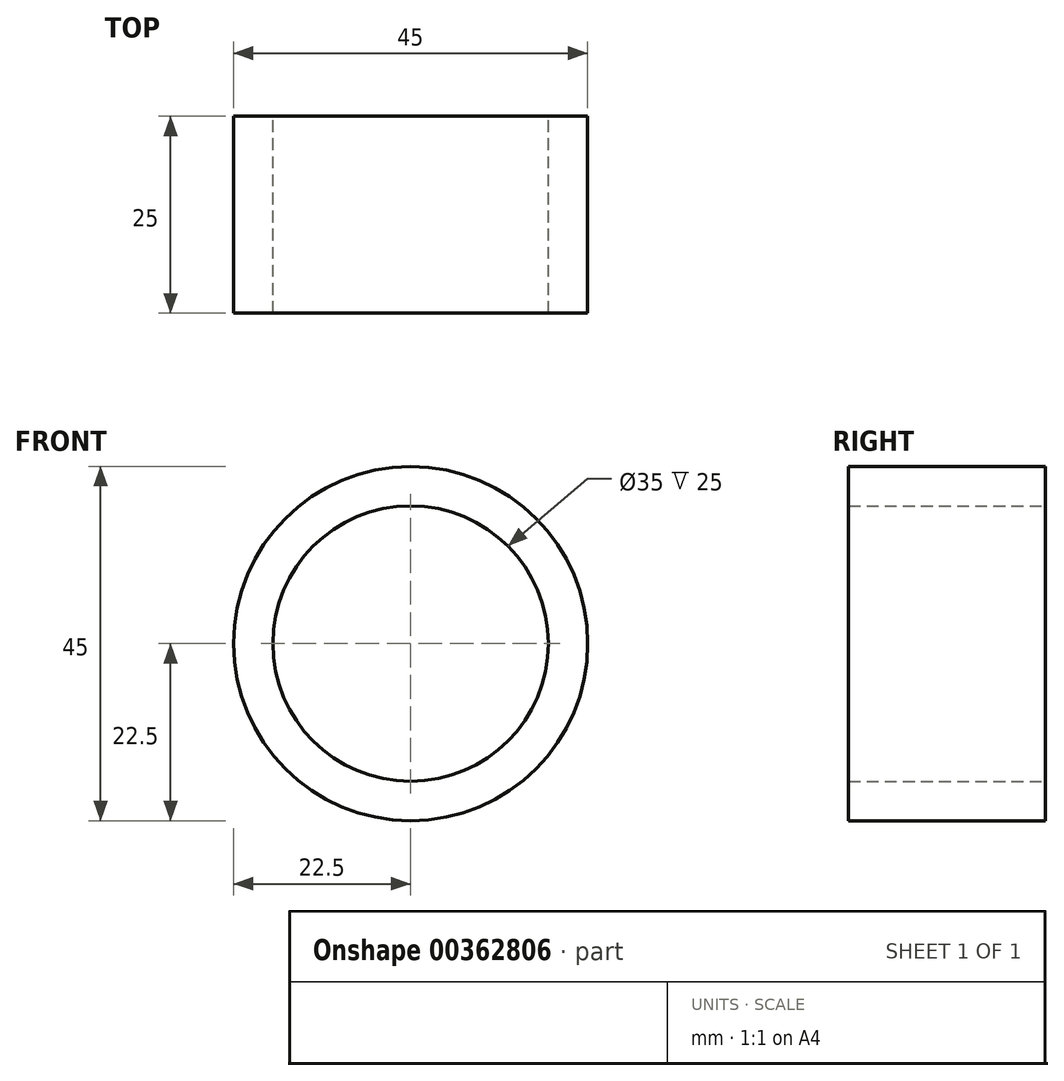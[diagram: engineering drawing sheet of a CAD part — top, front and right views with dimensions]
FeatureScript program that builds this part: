
annotation { "Feature Type Name" : "Feature", "Feature Type Description" : "" }
export const myFeature = defineFeature(function(context is Context, id is Id, definition is map)
    precondition{}
    {
        {
            var Q0;
            Q0=qCreatedBy(makeId("Front.planeOp"),FACE);
            var sketch = newSketch(context, id + "F0", { "sketchPlane" : qUnion([Q0])});
            skCircle(sketch, "E0", {"center": v(0, 0) * mm, "radius": 22.5 * mm});
            skCircle(sketch, "E1", {"center": v(0, 0) * mm, "radius": 17.5 * mm});
            skSolve(sketch);
        }
        {
            var Q0;
            Q0=makeQuery(id+"F0.imprint","IMPRINT",FACE,{"disambiguationData":[TD([[makeQuery(id+"F0.imprint","IMPRINT",EDGE,{"derivedFrom":sQuery(id+"F0.wireOp",EDGE,"E0")}),1.0]])]});
            extrude(context, id + "F1", {"entities" : qUnion([Q0]), "depth" : 25 * mm, "offsetDistance" : 25 * mm});
        }
    });
